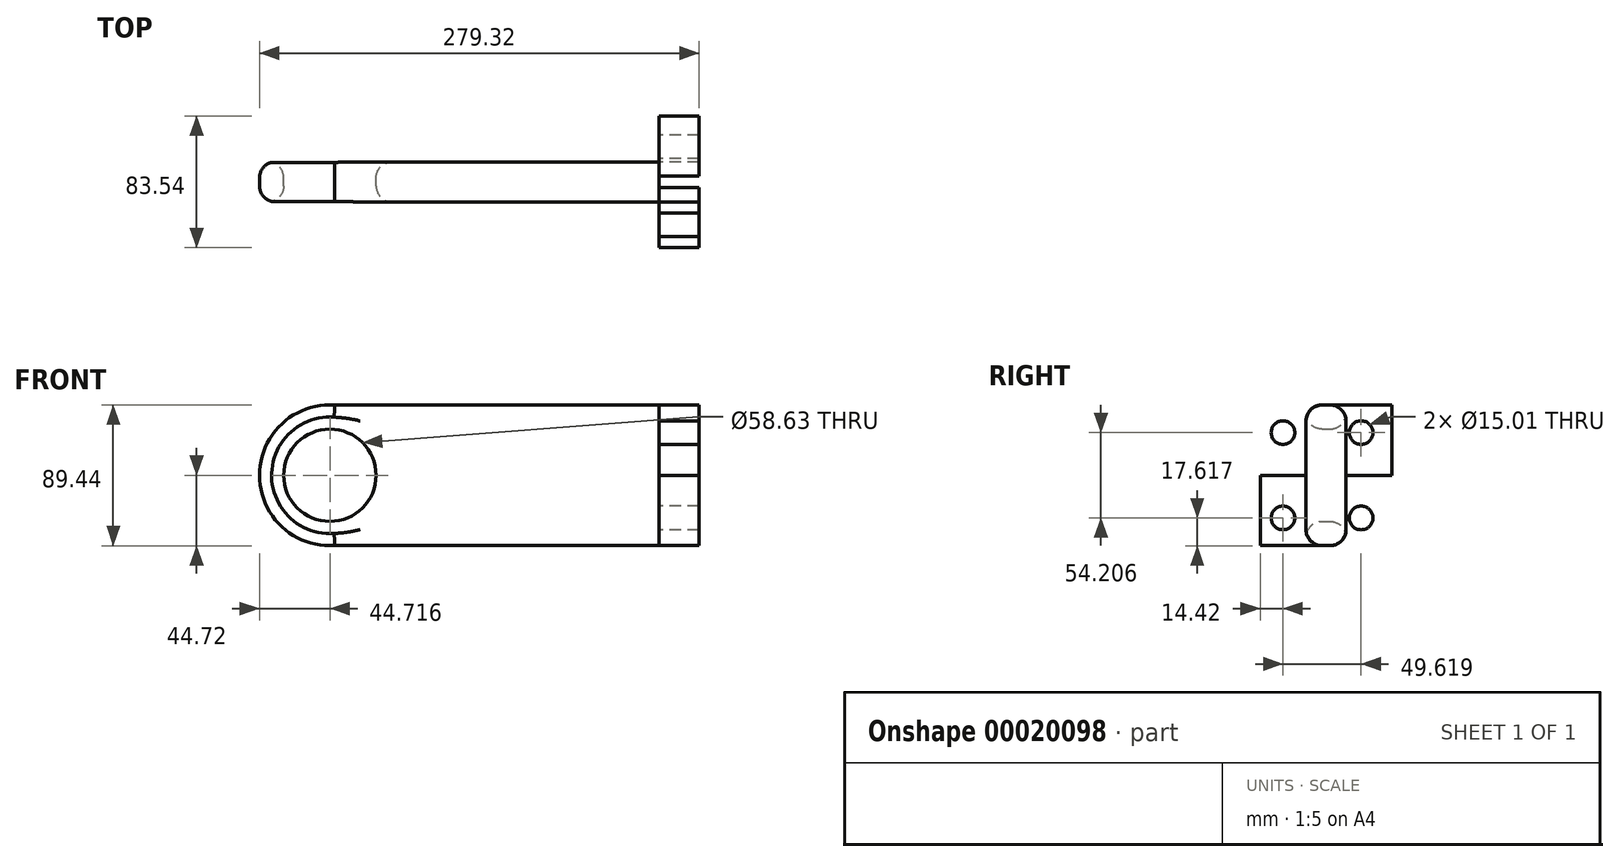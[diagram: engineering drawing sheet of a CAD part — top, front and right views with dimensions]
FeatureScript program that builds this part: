
annotation { "Feature Type Name" : "Feature", "Feature Type Description" : "" }
export const myFeature = defineFeature(function(context is Context, id is Id, definition is map)
    precondition{}
    {
        {
            var Q0;
            Q0=qCreatedBy(makeId("Front.planeOp"),FACE);
            var sketch = newSketch(context, id + "F0", { "sketchPlane" : qUnion([Q0])});
            skLineSegment(sketch, "E0.rect.bottom", {"start": v(-104.6, 44.62) * mm, "end": v(104.6, 44.62) * mm});
            skLineSegment(sketch, "E0.rect.top", {"start": v(-104.6, -44.62) * mm, "end": v(104.6, -44.62) * mm});
            skLineSegment(sketch, "E0.rect.left", {"start": v(-104.6, 44.62) * mm, "end": v(-104.6, -44.62) * mm});
            skLineSegment(sketch, "E0.rect.right", {"start": v(104.6, 44.62) * mm, "end": v(104.6, -44.62) * mm});
            skPoint(sketch, "E0.rect.middle", {"position": v(0, 0) * mm});
            skCircle(sketch, "E1", {"center": v(-104.6, 0) * mm, "radius": 44.72 * mm});
            skCircle(sketch, "E2", {"center": v(-104.6, 0) * mm, "radius": 29.32 * mm});
            skSolve(sketch);
        }
        {
            var Q0;
            {var subQ5=sQuery(id+"F0.wireOp",EDGE,"E0.rect.right");Q0=makeQuery(id+"F0.imprint","IMPRINT",FACE,{"disambiguationData":[TD([[makeQuery(id+"F0.imprint","IMPRINT",EDGE,{"derivedFrom":subQ5}),-1.0]])]});}
            var Q1;
            {var subQ1=sQuery(id+"F0.wireOp",EDGE,"E0.rect.left");var subQ7=sQuery(id+"F0.wireOp",EDGE,"E0.rect.bottom");var subQ10=makeQuery(id+"F0.imprint","INTERSECT",VERTEX,{"derivedFrom":[subQ7,subQ1]});Q1=makeQuery(id+"F0.imprint","IMPRINT",FACE,{"disambiguationData":[TD([[makeQuery(id+"F0.imprint","IMPRINT",EDGE,{"disambiguationData":[TD([[subQ10,-1.0]])],"derivedFrom":subQ7}),1.0]])]});}
            var Q2;
            {var subQ1=sQuery(id+"F0.wireOp",EDGE,"E0.rect.left");var subQ7=sQuery(id+"F0.wireOp",EDGE,"E0.rect.bottom");var subQ10=makeQuery(id+"F0.imprint","INTERSECT",VERTEX,{"derivedFrom":[subQ7,subQ1]});Q2=makeQuery(id+"F0.imprint","IMPRINT",FACE,{"disambiguationData":[TD([[makeQuery(id+"F0.imprint","IMPRINT",EDGE,{"disambiguationData":[TD([[subQ10,-1.0]])],"derivedFrom":subQ7}),-1.0]])]});}
            extrude(context, id + "F1", {"entities" : qUnion([Q0, Q1, Q2]), "depth" : 25.4 * mm});
        }
        {
            var Q0;
            Q0=makeQuery(id+"F1.opExtrude","CAP_EDGE",EDGE,{"disambiguationData":[OSD([sQuery(id+"F0.wireOp",EDGE,"E2")])],"isStart":false});
            var Q1;
            Q1=makeQuery(id+"F1.opExtrude","CAP_EDGE",EDGE,{"disambiguationData":[OSD([sQuery(id+"F0.wireOp",EDGE,"E1")])],"isStart":false});
            var Q2;
            Q2=makeQuery(id+"F1.opExtrude","CAP_EDGE",EDGE,{"disambiguationData":[OSD([sQuery(id+"F0.wireOp",EDGE,"E1")])],"isStart":true});
            var Q3;
            Q3=makeQuery(id+"F1.opExtrude","CAP_EDGE",EDGE,{"disambiguationData":[OSD([sQuery(id+"F0.wireOp",EDGE,"E2")])],"isStart":true});
            fillet(context, id + "F2", {"entities" : qUnion([Q0, Q1, Q2, Q3]), "radius" : 10.16 * mm, "tangentPropagation" : true, "allowEdgeOverflow" : false});
        }
        {
            var Q0;
            Q0=makeQuery(id+"F1.opExtrude","SWEPT_FACE",FACE,{"disambiguationData":[OSD([sQuery(id+"F0.wireOp",EDGE,"E0.rect.right")])]});
            var sketch = newSketch(context, id + "F3", { "sketchPlane" : qUnion([Q0])});
            skLineSegment(sketch, "E3", {"start": v(-25.4, 0) * mm, "end": v(0, 0) * mm});
            skLineSegment(sketch, "E4.rect.bottom", {"start": v(-54.47, 44.56) * mm, "end": v(29.07, 44.56) * mm});
            skLineSegment(sketch, "E4.rect.top", {"start": v(-54.47, -44.56) * mm, "end": v(29.07, -44.56) * mm});
            skLineSegment(sketch, "E4.rect.left", {"start": v(-54.47, 44.56) * mm, "end": v(-54.47, -44.56) * mm});
            skLineSegment(sketch, "E4.rect.right", {"start": v(29.07, 44.56) * mm, "end": v(29.07, -44.56) * mm});
            skPoint(sketch, "E4.rect.middle", {"position": v(-12.7, 0) * mm});
            skLineSegment(sketch, "E5", {"start": v(-54.47, 0) * mm, "end": v(29.07, 0) * mm});
            skLineSegment(sketch, "E6", {"start": v(-15.24, -44.62) * mm, "end": v(-15.24, 44.62) * mm});
            skCircle(sketch, "E7", {"center": v(-40.05, -27.1) * mm, "radius": 7.5 * mm});
            skCircle(sketch, "E8.MirrorC", {"center": v(-40.05, 27.1) * mm, "radius": 7.5 * mm});
            skCircle(sketch, "E9.MirrorC", {"center": v(9.57, -27.1) * mm, "radius": 7.5 * mm});
            skCircle(sketch, "E10.MirrorC", {"center": v(9.57, 27.1) * mm, "radius": 7.5 * mm});
            skSolve(sketch);
        }
        {
            var Q0;
            Q0=makeQuery(id+"F3.imprint","IMPRINT",FACE,{"disambiguationData":[TD([[makeQuery(id+"F3.imprint","IMPRINT",EDGE,{"derivedFrom":sQuery(id+"F3.wireOp",EDGE,"E9.MirrorC")}),1.0]])]});
            var Q1;
            Q1=makeQuery(id+"F3.imprint","IMPRINT",FACE,{"disambiguationData":[TD([[makeQuery(id+"F3.imprint","IMPRINT",EDGE,{"derivedFrom":sQuery(id+"F3.wireOp",EDGE,"E7")}),-1.0]])]});
            var Q2;
            Q2=makeQuery(id+"F3.imprint","IMPRINT",FACE,{"disambiguationData":[TD([[makeQuery(id+"F3.imprint","IMPRINT",EDGE,{"derivedFrom":sQuery(id+"F3.wireOp",EDGE,"E8.MirrorC")}),1.0]])]});
            var Q3;
            Q3=makeQuery(id+"F3.imprint","IMPRINT",FACE,{"disambiguationData":[TD([[makeQuery(id+"F3.imprint","IMPRINT",EDGE,{"derivedFrom":sQuery(id+"F3.wireOp",EDGE,"E10.MirrorC")}),-1.0]])]});
            extrude(context, id + "F4", {"entities" : qUnion([Q0, Q1, Q2, Q3]), "depth" : 25.4 * mm});
        }
    });
